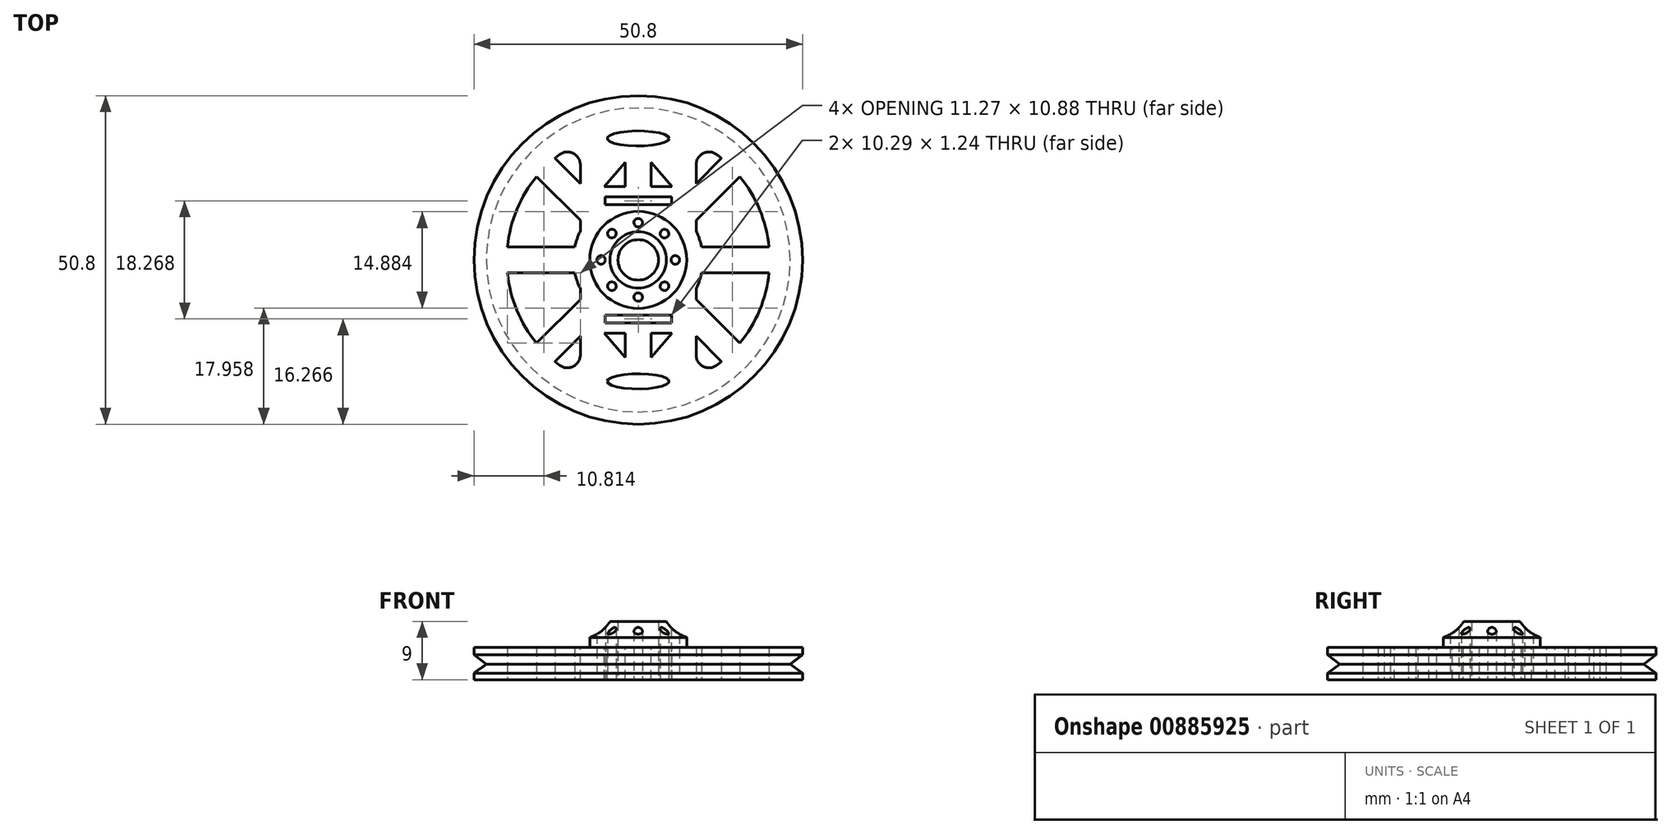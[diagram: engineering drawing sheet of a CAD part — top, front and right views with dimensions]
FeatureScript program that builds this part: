
annotation { "Feature Type Name" : "Feature", "Feature Type Description" : "" }
export const myFeature = defineFeature(function(context is Context, id is Id, definition is map)
    precondition{}
    {
        {
            var Q0;
            Q0=qCreatedBy(makeId("Top.planeOp"),FACE);
            var sketch = newSketch(context, id + "F0", { "sketchPlane" : qUnion([Q0])});
            skCircle(sketch, "E0", {"center": v(0, 0) * mm, "radius": 25.4 * mm});
            skCircle(sketch, "E1", {"center": v(0, 0) * mm, "radius": 3.12 * mm});
            skArc(sketch, "E2", {"start": v(-8.95, 4.46) * mm, "mid": v(-10, 0) * mm, "end": v(-8.95, -4.46) * mm});
            skArc(sketch, "E3.0", {"start": v(-12.15, 16.3) * mm, "mid": v(-20.32, 0) * mm, "end": v(-12.15, -16.3) * mm});
            skLineSegment(sketch, "E4.0", {"start": v(-8.95, 14.69) * mm, "end": v(-8.95, 4.46) * mm});
            skLineSegment(sketch, "E5.0", {"start": v(8.95, 14.69) * mm, "end": v(8.95, 4.46) * mm});
            skPoint(sketch, "E6.orphan", {"position": v(0, 22.46) * mm});
            skPoint(sketch, "E7.visualSharp", {"position": v(-8.95, 18.24) * mm});
            skArc(sketch, "E7.filletArc", {"start": v(-8.95, 14.69) * mm, "mid": v(-10.05, 16.47) * mm, "end": v(-12.15, 16.3) * mm});
            skPoint(sketch, "E8.visualSharp", {"position": v(8.95, 18.24) * mm});
            skArc(sketch, "E8.filletArc", {"start": v(12.15, 16.3) * mm, "mid": v(10.05, 16.47) * mm, "end": v(8.95, 14.69) * mm});
            skArc(sketch, "E9.1.0", {"start": v(-12.15, -16.3) * mm, "mid": v(-10.05, -16.47) * mm, "end": v(-8.95, -14.69) * mm});
            skArc(sketch, "E9.1.1", {"start": v(8.95, -14.69) * mm, "mid": v(10.05, -16.47) * mm, "end": v(12.15, -16.3) * mm});
            skLineSegment(sketch, "E9.1.2", {"start": v(8.95, -14.69) * mm, "end": v(8.95, -4.46) * mm});
            skLineSegment(sketch, "E9.1.3", {"start": v(-8.95, -14.69) * mm, "end": v(-8.95, -4.46) * mm});
            skArc(sketch, "E10.trimOffspring", {"start": v(12.15, -16.3) * mm, "mid": v(20.32, 0) * mm, "end": v(12.15, 16.3) * mm});
            skArc(sketch, "E11.trimOffspring", {"start": v(8.95, -4.46) * mm, "mid": v(10, 0) * mm, "end": v(8.95, 4.46) * mm});
            skSolve(sketch);
        }
        {
            var Q0;
            Q0=makeQuery(id+"F0.imprint","IMPRINT",FACE,{"disambiguationData":[TD([[makeQuery(id+"F0.imprint","IMPRINT",EDGE,{"derivedFrom":sQuery(id+"F0.wireOp",EDGE,"E0")}),1.0]])]});
            extrude(context, id + "F1", {"entities" : qUnion([Q0]), "depth" : 5 * mm, "offsetDistance" : 25.4 * mm});
        }
        {
            var Q0;
            Q0=makeQuery(id+"F1.opExtrude","CAP_FACE",FACE,{"disambiguationData":[OSD([sQuery(id+"F0.wireOp",EDGE,"E0"),sQuery(id+"F0.wireOp",EDGE,"E1"),sQuery(id+"F0.wireOp",EDGE,"E2"),sQuery(id+"F0.wireOp",EDGE,"E3.0"),sQuery(id+"F0.wireOp",EDGE,"E4.0"),sQuery(id+"F0.wireOp",EDGE,"E5.0"),sQuery(id+"F0.wireOp",EDGE,"E7.filletArc"),sQuery(id+"F0.wireOp",EDGE,"E8.filletArc"),sQuery(id+"F0.wireOp",EDGE,"E9.1.0"),sQuery(id+"F0.wireOp",EDGE,"E9.1.1"),sQuery(id+"F0.wireOp",EDGE,"E9.1.2"),sQuery(id+"F0.wireOp",EDGE,"E9.1.3"),sQuery(id+"F0.wireOp",EDGE,"E10.trimOffspring"),sQuery(id+"F0.wireOp",EDGE,"E11.trimOffspring")])],"isStart":false});
            var sketch = newSketch(context, id + "F2", { "sketchPlane" : qUnion([Q0])});
            skCircle(sketch, "E12", {"center": v(0, 0) * mm, "radius": 7.5 * mm});
            skSolve(sketch);
        }
        {
            var Q0;
            Q0=makeQuery(id+"F2.imprint","IMPRINT",FACE,{"disambiguationData":[TD([[makeQuery(id+"F2.imprint","IMPRINT",EDGE,{"derivedFrom":sQuery(id+"F2.wireOp",EDGE,"E12")}),1.0]])]});
            extrude(context, id + "F3", {"entities" : qUnion([Q0]), "operationType" : NewBodyOperationType.ADD, "depth" : 4 * mm, "offsetDistance" : 25.4 * mm});
        }
        {
            var Q0;
            Q0=qCreatedBy(makeId("Front.planeOp"),FACE);
            var sketch = newSketch(context, id + "F4", { "sketchPlane" : qUnion([Q0])});
            skCircle(sketch, "E13", {"center": v(-9.47, 12.31) * mm, "radius": 6.1 * mm});
            skLineSegment(sketch, "E14", {"start": v(0, 13.25) * mm, "end": v(0, -3.15) * mm, "construction": true});
            skSolve(sketch);
        }
        {
            var Q0;
            Q0=makeQuery(id+"F4.imprint","IMPRINT",FACE,{"disambiguationData":[TD([[makeQuery(id+"F4.imprint","IMPRINT",EDGE,{"derivedFrom":sQuery(id+"F4.wireOp",EDGE,"E13")}),1.0]])]});
            var Q1;
            Q1=sQuery(id+"F4.wireOp",EDGE,"E14");
            revolve(context, id + "F5", {"operationType" : NewBodyOperationType.REMOVE, "surfaceOperationType" : NewSurfaceOperationType.NEW, "entities" : qUnion([Q0]), "axis" : qUnion([Q1]), "revolveType" : RevolveType.FULL, "oppositeDirection" : true});
        }
        {
            var Q0;
            Q0=makeQuery(id+"F1.opExtrude","CAP_FACE",FACE,{"disambiguationData":[OSD([sQuery(id+"F0.wireOp",EDGE,"E0"),sQuery(id+"F0.wireOp",EDGE,"E1"),sQuery(id+"F0.wireOp",EDGE,"E2"),sQuery(id+"F0.wireOp",EDGE,"E3.0"),sQuery(id+"F0.wireOp",EDGE,"E4.0"),sQuery(id+"F0.wireOp",EDGE,"E5.0"),sQuery(id+"F0.wireOp",EDGE,"E7.filletArc"),sQuery(id+"F0.wireOp",EDGE,"E8.filletArc"),sQuery(id+"F0.wireOp",EDGE,"E9.1.0"),sQuery(id+"F0.wireOp",EDGE,"E9.1.1"),sQuery(id+"F0.wireOp",EDGE,"E9.1.2"),sQuery(id+"F0.wireOp",EDGE,"E9.1.3"),sQuery(id+"F0.wireOp",EDGE,"E10.trimOffspring"),sQuery(id+"F0.wireOp",EDGE,"E11.trimOffspring")])],"isStart":false});
            var sketch = newSketch(context, id + "F6", { "sketchPlane" : qUnion([Q0])});
            skLineSegment(sketch, "E15", {"start": v(0, 11.36) * mm, "end": v(-5.23, 11.36) * mm});
            skLineSegment(sketch, "E16", {"start": v(-5.23, 11.36) * mm, "end": v(0, 17.41) * mm});
            skLineSegment(sketch, "E17", {"start": v(0, 17.41) * mm, "end": v(0, 11.36) * mm});
            skLineSegment(sketch, "E18.MirrorCS", {"start": v(0, 11.36) * mm, "end": v(5.23, 11.36) * mm});
            skLineSegment(sketch, "E19.MirrorCS", {"start": v(5.23, 11.36) * mm, "end": v(0, 17.41) * mm});
            skLineSegment(sketch, "E20.1.0", {"start": v(-5.23, -11.36) * mm, "end": v(0, -17.41) * mm});
            skLineSegment(sketch, "E20.1.1", {"start": v(5.23, -11.36) * mm, "end": v(0, -17.41) * mm});
            skLineSegment(sketch, "E20.1.2", {"start": v(0, -11.36) * mm, "end": v(-5.23, -11.36) * mm});
            skLineSegment(sketch, "E20.1.3", {"start": v(0, -11.36) * mm, "end": v(5.23, -11.36) * mm});
            skPoint(sketch, "E20.center", {"position": v(0, 0) * mm});
            skSolve(sketch);
        }
        {
            var Q0;
            Q0=makeQuery(id+"F6.imprint","IMPRINT",FACE,{"disambiguationData":[TD([[makeQuery(id+"F6.imprint","IMPRINT",EDGE,{"derivedFrom":sQuery(id+"F6.wireOp",EDGE,"E17")}),1.0]])]});
            var Q1;
            Q1=makeQuery(id+"F6.imprint","IMPRINT",FACE,{"disambiguationData":[TD([[makeQuery(id+"F6.imprint","IMPRINT",EDGE,{"derivedFrom":sQuery(id+"F6.wireOp",EDGE,"E15")}),-1.0]])]});
            var Q2;
            Q2=makeQuery(id+"F6.imprint","IMPRINT",FACE,{"disambiguationData":[TD([[makeQuery(id+"F6.imprint","IMPRINT",EDGE,{"derivedFrom":sQuery(id+"F6.wireOp",EDGE,"E20.1.0")}),1.0]])]});
            extrude(context, id + "F7", {"entities" : qUnion([Q0, Q1, Q2]), "operationType" : NewBodyOperationType.REMOVE, "endBound" : BoundingType.THROUGH_ALL, "oppositeDirection" : true, "depth" : 25.4 * mm, "offsetDistance" : 25.4 * mm});
        }
        {
            var Q0;
            Q0=qCreatedBy(makeId("Front.planeOp"),FACE);
            var sketch = newSketch(context, id + "F8", { "sketchPlane" : qUnion([Q0])});
            skLineSegment(sketch, "E21", {"start": v(-25.5, 2.4) * mm, "end": v(-23.5, 2.4) * mm});
            skLineSegment(sketch, "E22", {"start": v(-23.5, 2.4) * mm, "end": v(-25.5, 0.9) * mm});
            skLineSegment(sketch, "E23", {"start": v(-25.5, 0.9) * mm, "end": v(-25.5, 2.4) * mm});
            skLineSegment(sketch, "E24.MirrorCS", {"start": v(-23.5, 2.4) * mm, "end": v(-25.5, 3.9) * mm});
            skLineSegment(sketch, "E25.MirrorCS", {"start": v(-25.5, 3.9) * mm, "end": v(-25.5, 2.4) * mm});
            skLineSegment(sketch, "E26", {"start": v(0, 41.08) * mm, "end": v(0, 0) * mm, "construction": true});
            skSolve(sketch);
        }
        {
            var Q0;
            Q0 = qSketchRegion(id + "F8", true);
            var Q1;
            Q1=sQuery(id+"F8.wireOp",EDGE,"E26");
            revolve(context, id + "F9", {"operationType" : NewBodyOperationType.REMOVE, "surfaceOperationType" : NewSurfaceOperationType.NEW, "entities" : qUnion([Q0]), "axis" : qUnion([Q1]), "revolveType" : RevolveType.FULL});
        }
        {
            var Q0;
            Q0=makeQuery(id+"F0.imprint","IMPRINT",FACE,{"disambiguationData":[TD([[makeQuery(id+"F0.imprint","IMPRINT",EDGE,{"derivedFrom":sQuery(id+"F0.wireOp",EDGE,"E5.0")}),1.0]])]});
            var sketch = newSketch(context, id + "F10", { "sketchPlane" : qUnion([Q0])});
            skCircle(sketch, "E27", {"center": v(0, 5.74) * mm, "radius": 0.66 * mm});
            skCircle(sketch, "E28.1.0", {"center": v(-4.06, 4.06) * mm, "radius": 0.66 * mm});
            skCircle(sketch, "E28.2.0", {"center": v(-5.74, 0) * mm, "radius": 0.66 * mm});
            skPoint(sketch, "E28.center", {"position": v(0, 0) * mm});
            skCircle(sketch, "E29.1.3.0", {"center": v(-4.06, -4.06) * mm, "radius": 0.66 * mm});
            skCircle(sketch, "E29.1.4.0", {"center": v(0, -5.74) * mm, "radius": 0.66 * mm});
            skCircle(sketch, "E29.1.5.0", {"center": v(4.06, -4.06) * mm, "radius": 0.66 * mm});
            skCircle(sketch, "E29.1.6.0", {"center": v(5.74, 0) * mm, "radius": 0.66 * mm});
            skCircle(sketch, "E30.1.7.0", {"center": v(4.06, 4.06) * mm, "radius": 0.66 * mm});
            skSolve(sketch);
        }
        {
            var Q0;
            Q0 = qSketchRegion(id + "F10", true);
            extrude(context, id + "F11", {"entities" : qUnion([Q0]), "operationType" : NewBodyOperationType.REMOVE, "endBound" : BoundingType.THROUGH_ALL, "depth" : 25.4 * mm, "offsetDistance" : 25.4 * mm});
        }
        {
            var Q0;
            Q0=qCreatedBy(makeId("Top.planeOp"),FACE);
            var sketch = newSketch(context, id + "F12", { "sketchPlane" : qUnion([Q0])});
            skLineSegment(sketch, "E31.0", {"start": v(-22.45, -2) * mm, "end": v(-8.8, -2) * mm});
            skLineSegment(sketch, "E32.0", {"start": v(-22.45, 2) * mm, "end": v(-8.8, 2) * mm});
            skPoint(sketch, "E33.start.orphan", {"position": v(-22.45, 0) * mm});
            skLineSegment(sketch, "E34", {"start": v(-8.8, -2) * mm, "end": v(-8.8, 2) * mm});
            skLineSegment(sketch, "E35", {"start": v(-22.45, -2) * mm, "end": v(-22.45, 2) * mm});
            skLineSegment(sketch, "E36.1.0", {"start": v(-4.8, -7.64) * mm, "end": v(-7.64, -4.8) * mm});
            skLineSegment(sketch, "E36.1.1", {"start": v(-14.46, -17.29) * mm, "end": v(-4.8, -7.64) * mm});
            skLineSegment(sketch, "E36.1.2", {"start": v(-17.29, -14.46) * mm, "end": v(-7.64, -4.8) * mm});
            skLineSegment(sketch, "E36.1.3", {"start": v(-14.46, -17.29) * mm, "end": v(-17.29, -14.46) * mm});
            skLineSegment(sketch, "E36.2.0", {"start": v(2, -8.8) * mm, "end": v(-2, -8.8) * mm});
            skLineSegment(sketch, "E36.2.1", {"start": v(2, -22.45) * mm, "end": v(2, -8.8) * mm});
            skLineSegment(sketch, "E36.2.2", {"start": v(-2, -22.45) * mm, "end": v(-2, -8.8) * mm});
            skLineSegment(sketch, "E36.2.3", {"start": v(2, -22.45) * mm, "end": v(-2, -22.45) * mm});
            skPoint(sketch, "E36.center", {"position": v(0, 0) * mm});
            skLineSegment(sketch, "E37.1.3.0", {"start": v(7.64, -4.8) * mm, "end": v(4.8, -7.64) * mm});
            skLineSegment(sketch, "E37.3.3.0", {"start": v(17.29, -14.46) * mm, "end": v(7.64, -4.8) * mm});
            skLineSegment(sketch, "E37.6.3.0", {"start": v(14.46, -17.29) * mm, "end": v(4.8, -7.64) * mm});
            skLineSegment(sketch, "E37.9.3.0", {"start": v(17.29, -14.46) * mm, "end": v(14.46, -17.29) * mm});
            skLineSegment(sketch, "E38.1.4.0", {"start": v(8.8, 2) * mm, "end": v(8.8, -2) * mm});
            skLineSegment(sketch, "E38.3.4.0", {"start": v(22.45, 2) * mm, "end": v(8.8, 2) * mm});
            skLineSegment(sketch, "E38.6.4.0", {"start": v(22.45, -2) * mm, "end": v(8.8, -2) * mm});
            skLineSegment(sketch, "E38.9.4.0", {"start": v(22.45, 2) * mm, "end": v(22.45, -2) * mm});
            skLineSegment(sketch, "E38.1.5.0", {"start": v(4.8, 7.64) * mm, "end": v(7.64, 4.8) * mm});
            skLineSegment(sketch, "E38.3.5.0", {"start": v(14.46, 17.29) * mm, "end": v(4.8, 7.64) * mm});
            skLineSegment(sketch, "E38.6.5.0", {"start": v(17.29, 14.46) * mm, "end": v(7.64, 4.8) * mm});
            skLineSegment(sketch, "E38.9.5.0", {"start": v(14.46, 17.29) * mm, "end": v(17.29, 14.46) * mm});
            skLineSegment(sketch, "E39.1.6.0", {"start": v(-2, 8.8) * mm, "end": v(2, 8.8) * mm});
            skLineSegment(sketch, "E39.3.6.0", {"start": v(-2, 22.45) * mm, "end": v(-2, 8.8) * mm});
            skLineSegment(sketch, "E39.6.6.0", {"start": v(2, 22.45) * mm, "end": v(2, 8.8) * mm});
            skLineSegment(sketch, "E39.9.6.0", {"start": v(-2, 22.45) * mm, "end": v(2, 22.45) * mm});
            skLineSegment(sketch, "E39.1.7.0", {"start": v(-7.64, 4.8) * mm, "end": v(-4.8, 7.64) * mm});
            skLineSegment(sketch, "E39.3.7.0", {"start": v(-17.29, 14.46) * mm, "end": v(-7.64, 4.8) * mm});
            skLineSegment(sketch, "E39.6.7.0", {"start": v(-14.46, 17.29) * mm, "end": v(-4.8, 7.64) * mm});
            skLineSegment(sketch, "E39.9.7.0", {"start": v(-17.29, 14.46) * mm, "end": v(-14.46, 17.29) * mm});
            skSolve(sketch);
        }
        {
            var Q0;
            Q0 = qSketchRegion(id + "F12", true);
            extrude(context, id + "F13", {"entities" : qUnion([Q0]), "operationType" : NewBodyOperationType.ADD, "depth" : 5 * mm, "offsetDistance" : 25.4 * mm});
        }
        {
            var Q0;
            Q0=qCreatedBy(makeId("Top.planeOp"),FACE);
            var sketch = newSketch(context, id + "F14", { "sketchPlane" : qUnion([Q0])});
            skEllipse(sketch, "E40", {"center": v(0, 18.77) * mm, "majorRadius": 4.8 * mm, "minorRadius": 1.17 * mm, "majorAxis": v(1, 0)});
            skEllipse(sketch, "E41.1.0", {"center": v(0, -18.77) * mm, "majorRadius": 4.8 * mm, "minorRadius": 1.17 * mm, "majorAxis": v(-1, 0)});
            skPoint(sketch, "E41.center", {"position": v(0, 0) * mm});
            skSolve(sketch);
        }
        {
            var Q0;
            Q0 = qSketchRegion(id + "F14", true);
            extrude(context, id + "F15", {"entities" : qUnion([Q0]), "operationType" : NewBodyOperationType.REMOVE, "endBound" : BoundingType.SYMMETRIC, "oppositeDirection" : true, "depth" : 25.4 * mm, "offsetDistance" : 25.4 * mm});
        }
        {
            var Q0;
            Q0=qCreatedBy(makeId("Top.planeOp"),FACE);
            var sketch = newSketch(context, id + "F16", { "sketchPlane" : qUnion([Q0])});
            skLineSegment(sketch, "E42.bottom", {"start": v(5.15, 9.76) * mm, "end": v(-5.15, 9.76) * mm});
            skLineSegment(sketch, "E42.top", {"start": v(5.15, 8.51) * mm, "end": v(-5.15, 8.51) * mm});
            skLineSegment(sketch, "E42.left", {"start": v(5.15, 9.76) * mm, "end": v(5.15, 8.51) * mm});
            skLineSegment(sketch, "E42.right", {"start": v(-5.15, 9.76) * mm, "end": v(-5.15, 8.51) * mm});
            skPoint(sketch, "E42.middle", {"position": v(0, 9.13) * mm});
            skLineSegment(sketch, "E43.1.0", {"start": v(-5.15, -9.76) * mm, "end": v(-5.15, -8.51) * mm});
            skLineSegment(sketch, "E43.1.1", {"start": v(5.15, -9.76) * mm, "end": v(5.15, -8.51) * mm});
            skLineSegment(sketch, "E43.1.2", {"start": v(-5.15, -8.51) * mm, "end": v(5.15, -8.51) * mm});
            skLineSegment(sketch, "E43.1.3", {"start": v(-5.15, -9.76) * mm, "end": v(5.15, -9.76) * mm});
            skPoint(sketch, "E43.center", {"position": v(0, 0) * mm});
            skSolve(sketch);
        }
        {
            var Q0;
            Q0 = qSketchRegion(id + "F16", true);
            extrude(context, id + "F17", {"entities" : qUnion([Q0]), "operationType" : NewBodyOperationType.REMOVE, "endBound" : BoundingType.SYMMETRIC, "oppositeDirection" : true, "depth" : 25.4 * mm, "offsetDistance" : 25.4 * mm});
        }
    });
